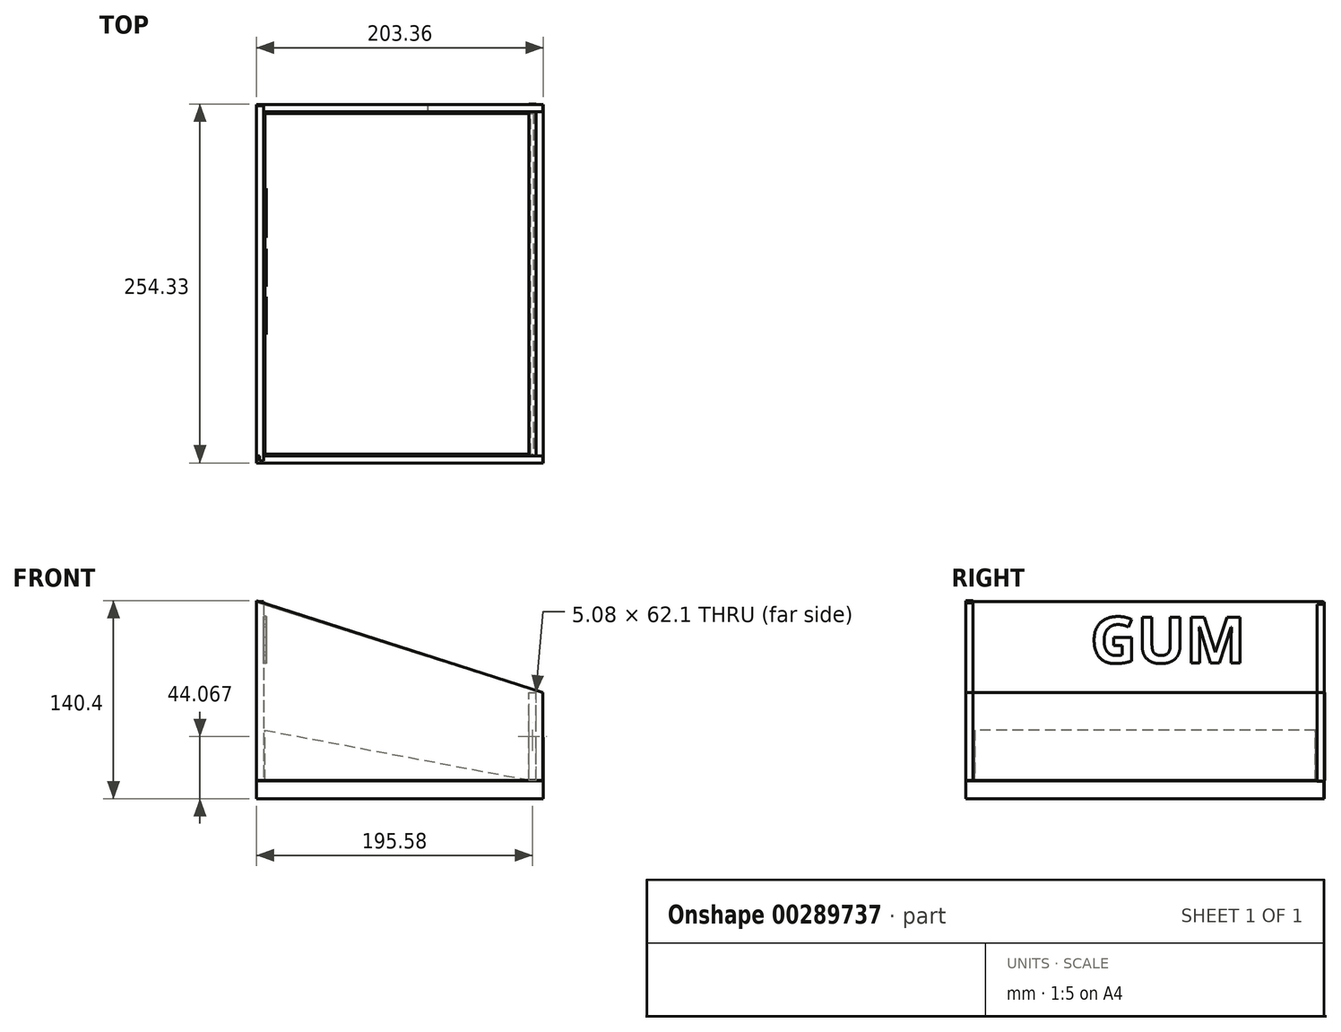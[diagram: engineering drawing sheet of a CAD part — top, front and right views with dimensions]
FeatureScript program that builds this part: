
annotation { "Feature Type Name" : "Feature", "Feature Type Description" : "" }
export const myFeature = defineFeature(function(context is Context, id is Id, definition is map)
    precondition{}
    {
        {
            var Q0;
            Q0=qCreatedBy(makeId("Top.planeOp"),FACE);
            var sketch = newSketch(context, id + "F0", { "sketchPlane" : qUnion([Q0])});
            skLineSegment(sketch, "E0", {"start": v(0, 0) * mm, "end": v(0, -127) * mm});
            skLineSegment(sketch, "E1", {"start": v(0, 0) * mm, "end": v(0, 127) * mm});
            skLineSegment(sketch, "E2", {"start": v(0, -127) * mm, "end": v(203.2, -127) * mm});
            skLineSegment(sketch, "E3", {"start": v(0, 127) * mm, "end": v(203.2, 126.72) * mm});
            skLineSegment(sketch, "E4", {"start": v(203.2, 126.72) * mm, "end": v(203.2, -127) * mm});
            skSolve(sketch);
        }
        {
            var Q0;
            Q0=makeQuery(id+"F0.imprint","IMPRINT",FACE,{"disambiguationData":[TD([[makeQuery(id+"F0.imprint","IMPRINT",EDGE,{"derivedFrom":sQuery(id+"F0.wireOp",EDGE,"E0")}),1.0]])]});
            extrude(context, id + "F1", {"entities" : qUnion([Q0]), "depth" : 12.7 * mm});
        }
        {
            var Q0;
            Q0=qCreatedBy(makeId("Right.planeOp"),FACE);
            var sketch = newSketch(context, id + "F2", { "sketchPlane" : qUnion([Q0])});
            skLineSegment(sketch, "E5", {"start": v(-125.57, 12.68) * mm, "end": v(-125.57, 139.68) * mm});
            skLineSegment(sketch, "E6", {"start": v(125.54, 12.68) * mm, "end": v(125.54, 112.06) * mm});
            skLineSegment(sketch, "E7", {"start": v(-125.57, 139.68) * mm, "end": v(126.21, 139.68) * mm});
            skLineSegment(sketch, "E8", {"start": v(125.54, 112.06) * mm, "end": v(126.21, 139.68) * mm});
            skLineSegment(sketch, "E9", {"start": v(-125.57, 12.68) * mm, "end": v(125.54, 12.68) * mm});
            skSolve(sketch);
        }
        {
            var Q0;
            Q0=makeQuery(id+"F2.imprint","IMPRINT",FACE,{"disambiguationData":[TD([[makeQuery(id+"F2.imprint","IMPRINT",EDGE,{"derivedFrom":sQuery(id+"F2.wireOp",EDGE,"E5")}),-1.0]])]});
            extrude(context, id + "F3", {"entities" : qUnion([Q0]), "operationType" : NewBodyOperationType.ADD, "depth" : 5.08 * mm});
        }
        {
            var Q0;
            Q0=qCreatedBy(makeId("Front.planeOp"),FACE);
            cPlane(context, id + "F4", {"entities" : qUnion([Q0]), "cplaneType" : CPlaneType.OFFSET, "offset" : 127 * mm, "width" : 152.4 * mm, "height" : 152.4 * mm});
        }
        {
            var Q0;
            Q0=qCreatedBy(id+"F4.planeOp",FACE);
            var sketch = newSketch(context, id + "F5", { "sketchPlane" : qUnion([Q0])});
            skLineSegment(sketch, "E10", {"start": v(0, 140.4) * mm, "end": v(0, 13.02) * mm});
            skLineSegment(sketch, "E11", {"start": v(0, 13.02) * mm, "end": v(202.83, 13.02) * mm});
            skLineSegment(sketch, "E12", {"start": v(202.83, 13.02) * mm, "end": v(202.83, 75.12) * mm});
            skLineSegment(sketch, "E13", {"start": v(202.83, 75.12) * mm, "end": v(0, 140.4) * mm});
            skSolve(sketch);
        }
        {
            var Q0;
            Q0=makeQuery(id+"F5.imprint","IMPRINT",FACE,{"disambiguationData":[TD([[makeQuery(id+"F5.imprint","IMPRINT",EDGE,{"derivedFrom":sQuery(id+"F5.wireOp",EDGE,"E10")}),1.0]])]});
            extrude(context, id + "F6", {"entities" : qUnion([Q0]), "operationType" : NewBodyOperationType.ADD, "oppositeDirection" : true, "depth" : 5.08 * mm});
        }
        {
            var Q0;
            Q0=qCreatedBy(makeId("Front.planeOp"),FACE);
            cPlane(context, id + "F7", {"entities" : qUnion([Q0]), "cplaneType" : CPlaneType.OFFSET, "offset" : 127 * mm, "oppositeDirection" : true, "width" : 152.4 * mm, "height" : 152.4 * mm});
        }
        {
            var Q0;
            Q0=qCreatedBy(id+"F7.planeOp",FACE);
            var sketch = newSketch(context, id + "F8", { "sketchPlane" : qUnion([Q0])});
            skLineSegment(sketch, "E14", {"start": v(0, 139.34) * mm, "end": v(0, 13.02) * mm});
            skLineSegment(sketch, "E15", {"start": v(0, 13.02) * mm, "end": v(203.36, 12.49) * mm});
            skLineSegment(sketch, "E16", {"start": v(0, 139.34) * mm, "end": v(202.83, 75.12) * mm});
            skLineSegment(sketch, "E17", {"start": v(203.36, 12.49) * mm, "end": v(202.83, 75.12) * mm});
            skSolve(sketch);
        }
        {
            var Q0;
            Q0=makeQuery(id+"F8.imprint","IMPRINT",FACE,{"disambiguationData":[TD([[makeQuery(id+"F8.imprint","IMPRINT",EDGE,{"derivedFrom":sQuery(id+"F8.wireOp",EDGE,"E14")}),1.0]])]});
            extrude(context, id + "F9", {"entities" : qUnion([Q0]), "operationType" : NewBodyOperationType.ADD, "depth" : 5.08 * mm});
        }
        {
            var Q0;
            Q0=qCreatedBy(makeId("Right.planeOp"),FACE);
            cPlane(context, id + "F10", {"entities" : qUnion([Q0]), "cplaneType" : CPlaneType.OFFSET, "offset" : 198.12 * mm, "width" : 152.4 * mm, "height" : 152.4 * mm});
        }
        {
            var Q0;
            Q0=qCreatedBy(id+"F10.planeOp",FACE);
            var sketch = newSketch(context, id + "F11", { "sketchPlane" : qUnion([Q0])});
            skLineSegment(sketch, "E18", {"start": v(-126.9, 75.12) * mm, "end": v(127.33, 75.12) * mm});
            skLineSegment(sketch, "E19", {"start": v(-126.9, 75.12) * mm, "end": v(-126.9, 13.02) * mm});
            skLineSegment(sketch, "E20", {"start": v(-126.9, 13.02) * mm, "end": v(127.33, 13.02) * mm});
            skLineSegment(sketch, "E21", {"start": v(127.33, 75.12) * mm, "end": v(127.33, 13.02) * mm});
            skSolve(sketch);
        }
        {
            var Q0;
            Q0=makeQuery(id+"F11.imprint","IMPRINT",FACE,{"disambiguationData":[TD([[makeQuery(id+"F11.imprint","IMPRINT",EDGE,{"derivedFrom":sQuery(id+"F11.wireOp",EDGE,"E18")}),-1.0]])]});
            extrude(context, id + "F12", {"entities" : qUnion([Q0]), "operationType" : NewBodyOperationType.ADD, "oppositeDirection" : true, "depth" : 5.08 * mm});
        }
        {
            var Q0;
            Q0=qCreatedBy(id+"F4.planeOp",FACE);
            cPlane(context, id + "F13", {"entities" : qUnion([Q0]), "cplaneType" : CPlaneType.OFFSET, "offset" : 6.35 * mm, "oppositeDirection" : true, "width" : 152.4 * mm, "height" : 152.4 * mm});
        }
        {
            var Q0;
            Q0=qCreatedBy(id+"F13.planeOp",FACE);
            var sketch = newSketch(context, id + "F14", { "sketchPlane" : qUnion([Q0])});
            skLineSegment(sketch, "E22", {"start": v(5.94, 12.3) * mm, "end": v(167.8, 12.3) * mm});
            skLineSegment(sketch, "E23", {"start": v(5.94, 12.3) * mm, "end": v(198.2, 12.3) * mm});
            skLineSegment(sketch, "E24", {"start": v(5.94, 12.3) * mm, "end": v(5.94, 48.64) * mm});
            skLineSegment(sketch, "E25", {"start": v(5.94, 48.64) * mm, "end": v(198.2, 12.3) * mm});
            skSolve(sketch);
        }
        {
            var Q0;
            {var subQ0=sQuery(id+"F14.wireOp",EDGE,"E24");Q0=makeQuery(id+"F14.imprint","IMPRINT",FACE,{"disambiguationData":[TD([[makeQuery(id+"F14.imprint","IMPRINT",EDGE,{"derivedFrom":subQ0}),-1.0]])]});}
            extrude(context, id + "F15", {"entities" : qUnion([Q0]), "operationType" : NewBodyOperationType.ADD, "oppositeDirection" : true, "depth" : 241.3 * mm});
        }
        {
            var Q0;
            Q0=qCreatedBy(makeId("Right.planeOp"),FACE);
            var sketch = newSketch(context, id + "F16", { "sketchPlane" : qUnion([Q0])});
            skText(sketch, "E26", { "text": "GUM", "fontName": "OpenSans-Bold.ttf"});
            const initialGuessF16  = {"E26": [-0.03867, 0.09622, 1, 0, 0.03276]};
            skSetInitialGuess(sketch, initialGuessF16);
            skSolve(sketch);
        }
        {
            var Q0;
            Q0 = qSketchRegion(id + "F16", true);
            extrude(context, id + "F17", {"entities" : qUnion([Q0]), "operationType" : NewBodyOperationType.ADD, "depth" : 6.86 * mm});
        }
    });
